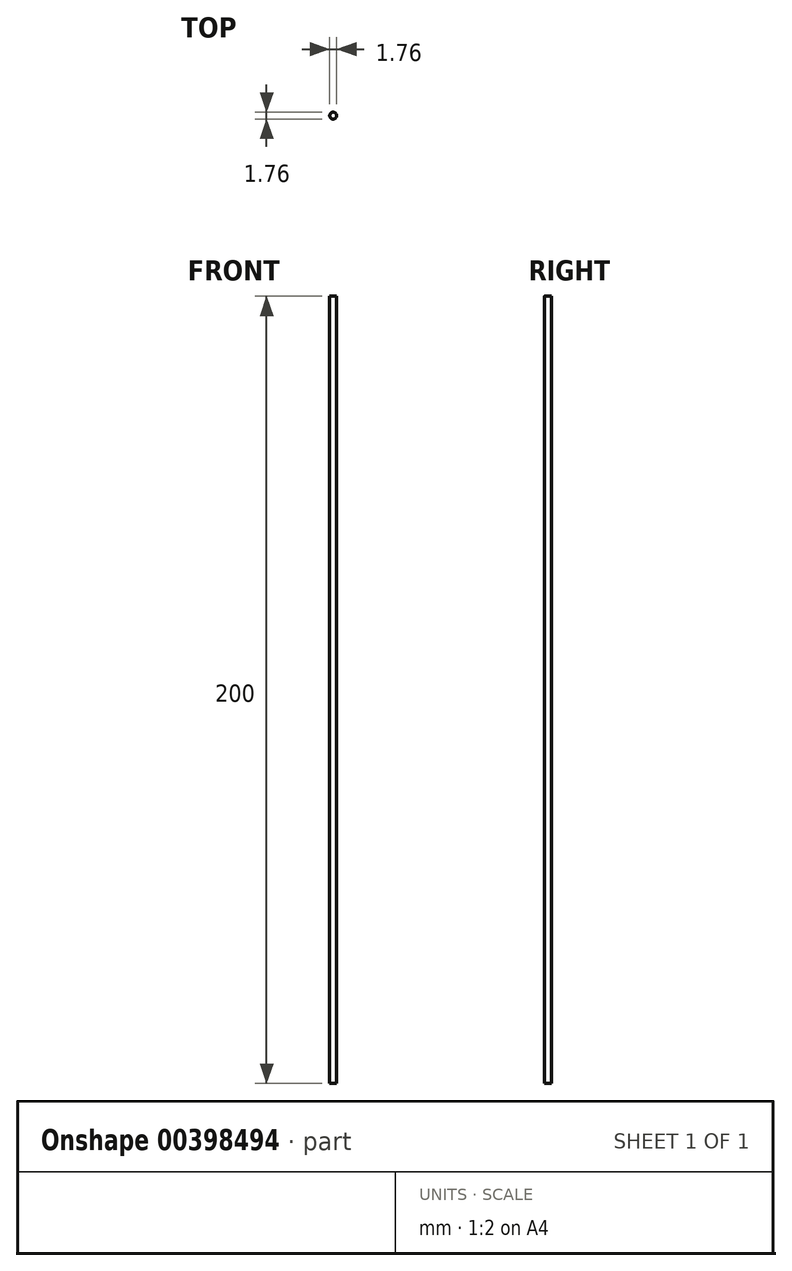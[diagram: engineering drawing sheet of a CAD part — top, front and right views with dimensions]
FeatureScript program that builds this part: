
annotation { "Feature Type Name" : "Feature", "Feature Type Description" : "" }
export const myFeature = defineFeature(function(context is Context, id is Id, definition is map)
    precondition{}
    {
        {
            var Q0;
            Q0=qCreatedBy(makeId("Top.planeOp"),FACE);
            var sketch = newSketch(context, id + "F0", { "sketchPlane" : qUnion([Q0])});
            skCircle(sketch, "E0", {"center": v(0, 0) * mm, "radius": 0.88 * mm});
            skSolve(sketch);
        }
        {
            var Q0;
            Q0 = qSketchRegion(id + "F0", true);
            extrude(context, id + "F1", {"entities" : qUnion([Q0]), "endBound" : BoundingType.SYMMETRIC, "depth" : 200 * mm});
        }
    });
